# Revit family: DAL_A3-Swartland-Winsters-doubleStable-PD1S
name_source: partatom
category: Doors
revit_build: Autodesk Revit 2016 (Build: 20150220_1215(x64)
units: mm (PartAtom-declared; Revit-internal decimal feet)

## family parameters
Always vertical = Yes
Cut with Voids When Loaded = No
Host = Wall
Room Calculation Point = No
Shared = No

## types (1)
- 813w X 2032h
    Assembly Code = B2030230
    Construction Type = Timber
    Frame Width = 33 mm  [stored 0.108268 ft]
    Function = Interior
    Height = 2032 mm  [stored 6.66667 ft]
    Manufacturer = Swartland
    Manufacturer Code = PD1S
    Material Door Frame = Default Timber Door Frame
    Material Door Panel = Default Timber Door Panel
    Model = Winsters
    Model Type = Single Stable Door
    Rough Height = 2065 mm  [stored 6.77493 ft]
    Rough Width = 879 mm  [stored 2.88386 ft]
    Thickness = 0 mm  [stored 0 ft]
    URL = http://www.swartland.co.za
    Wall Closure = By host
    Width = 813 mm  [stored 2.66732 ft]

note: [stored X ft] marks values corroborated as IEEE doubles in the binary element streams (Revit-internal decimal feet)

## geometry (parser evidence)
native form markers: Sweep x4
no freeform markers — native parametric forms only
